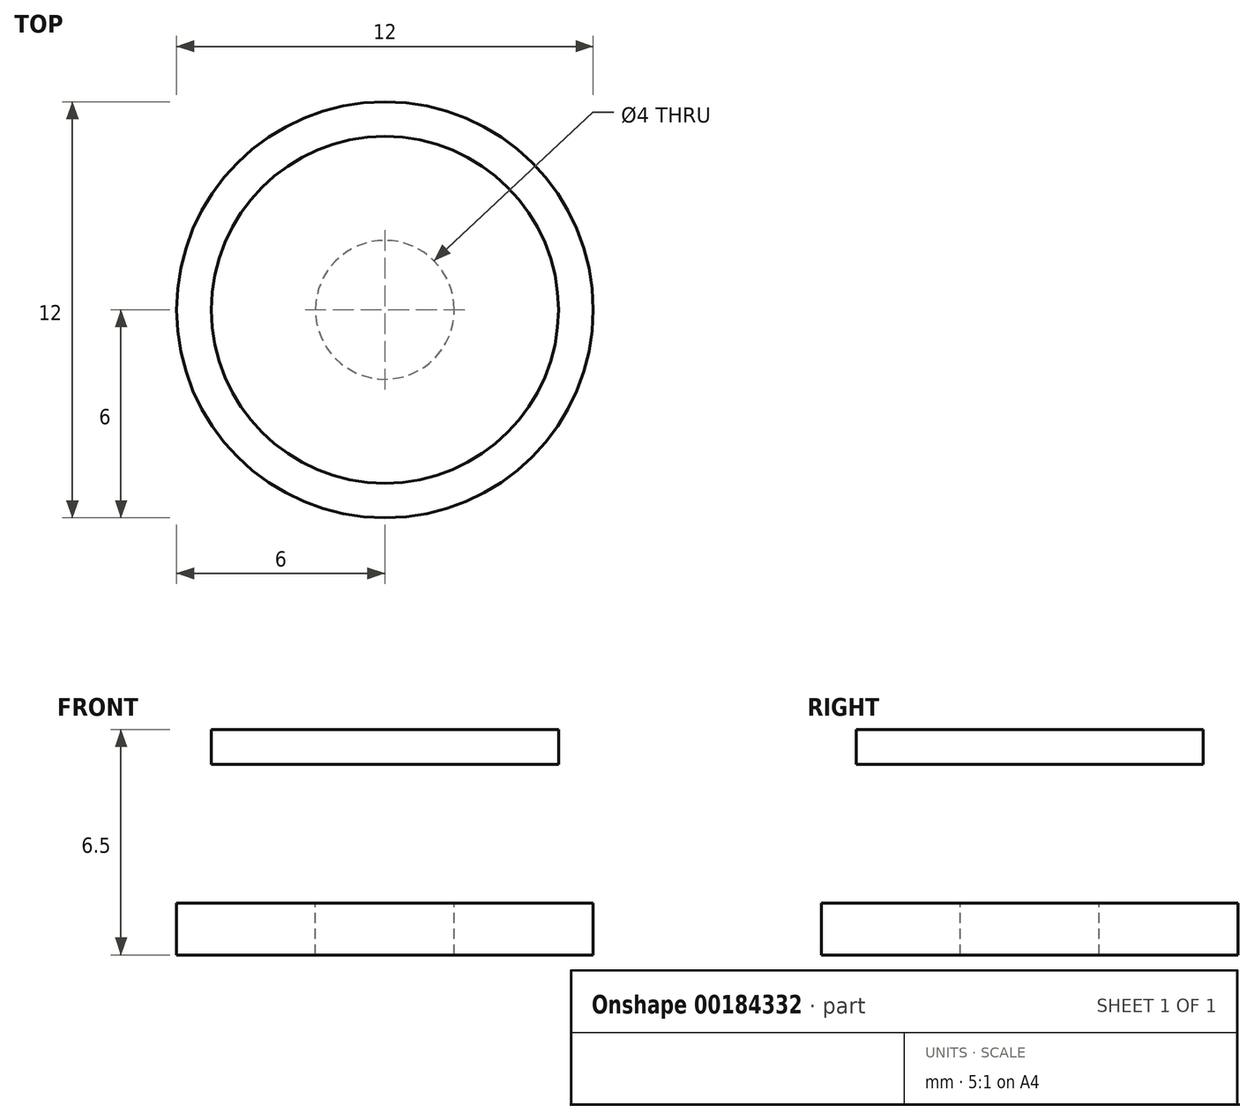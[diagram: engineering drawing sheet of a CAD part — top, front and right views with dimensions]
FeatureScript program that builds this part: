
annotation { "Feature Type Name" : "Feature", "Feature Type Description" : "" }
export const myFeature = defineFeature(function(context is Context, id is Id, definition is map)
    precondition{}
    {
        {
            var Q0;
            Q0=qCreatedBy(makeId("Right.planeOp"),FACE);
            var sketch = newSketch(context, id + "F0", { "sketchPlane" : qUnion([Q0])});
            skLineSegment(sketch, "E0.bottom", {"start": v(0, 0) * mm, "end": v(6, 0) * mm});
            skLineSegment(sketch, "E0.top", {"start": v(0, -1.5) * mm, "end": v(6, -1.5) * mm});
            skLineSegment(sketch, "E0.left", {"start": v(0, 0) * mm, "end": v(0, -1.5) * mm});
            skLineSegment(sketch, "E0.right", {"start": v(6, 0) * mm, "end": v(6, -1.5) * mm});
            skLineSegment(sketch, "E1.bottom", {"start": v(0, 0) * mm, "end": v(5, 0) * mm});
            skLineSegment(sketch, "E1.left", {"start": v(0, 0) * mm, "end": v(0, 4) * mm});
            skLineSegment(sketch, "E1.right", {"start": v(5, 0) * mm, "end": v(5, 4) * mm});
            skArc(sketch, "E2", {"start": v(5, 4) * mm, "mid": v(3, 2) * mm, "end": v(5, 0) * mm});
            skLineSegment(sketch, "E3.top", {"start": v(0, 5) * mm, "end": v(5, 5) * mm});
            skLineSegment(sketch, "E3.left", {"start": v(0, 4) * mm, "end": v(0, 5) * mm});
            skLineSegment(sketch, "E4", {"start": v(5, 4) * mm, "end": v(5, 5) * mm});
            skLineSegment(sketch, "E5", {"start": v(0, 4) * mm, "end": v(5, 4) * mm});
            skSolve(sketch);
        }
        {
            var Q0;
            Q0=makeQuery(id+"F0.imprint","IMPRINT",FACE,{"disambiguationData":[TD([[makeQuery(id+"F0.imprint","IMPRINT",EDGE,{"derivedFrom":sQuery(id+"F0.wireOp",EDGE,"E0.bottom")}),-1.0]])]});
            var Q1;
            Q1=makeQuery(id+"F0.imprint","IMPRINT",FACE,{"disambiguationData":[TD([[makeQuery(id+"F0.imprint","IMPRINT",EDGE,{"derivedFrom":sQuery(id+"F0.wireOp",EDGE,"E1.bottom")}),1.0]])]});
            var Q2;
            Q2=makeQuery(id+"F0.imprint","IMPRINT",FACE,{"disambiguationData":[TD([[makeQuery(id+"F0.imprint","IMPRINT",EDGE,{"derivedFrom":sQuery(id+"F0.wireOp",EDGE,"E3.top")}),-1.0]])]});
            var Q3;
            Q3=sQuery(id+"F0.wireOp",EDGE,"E1.left");
            revolve(context, id + "F1", {"entities" : qUnion([Q0, Q1, Q2]), "axis" : qUnion([Q3]), "revolveType" : RevolveType.FULL});
        }
        {
            var Q0;
            Q0=makeQuery(id+"F1.opRevolve","SWEPT_FACE",FACE,{"disambiguationData":[OSD([sQuery(id+"F0.wireOp",EDGE,"E3.top")])]});
            var sketch = newSketch(context, id + "F2", { "sketchPlane" : qUnion([Q0])});
            skPoint(sketch, "E6", {"position": v(0, 0) * mm});
            skSolve(sketch);
        }
        {
            var Q0;
            Q0=sQuery(id+"F2.wireOp",VERTEX,"E6");
            var Q1;
            Q1=makeQuery(id+"F1.opRevolve","SWEPT_BODY",BODY,{"disambiguationData":[OSD([sQuery(id+"F0.wireOp",EDGE,"E0.bottom"),sQuery(id+"F0.wireOp",EDGE,"E0.top"),sQuery(id+"F0.wireOp",EDGE,"E0.left"),sQuery(id+"F0.wireOp",EDGE,"E0.right"),sQuery(id+"F0.wireOp",EDGE,"E1.left"),sQuery(id+"F0.wireOp",EDGE,"E2"),sQuery(id+"F0.wireOp",EDGE,"E3.top"),sQuery(id+"F0.wireOp",EDGE,"E3.left"),sQuery(id+"F0.wireOp",EDGE,"E4")])]});
            hole(context, id + "F3", {"style" : HoleStyle.SIMPLE, "endStyle" : HoleEndStyle.THROUGH, "holeDiameter" : 4 * mm, "locations" : qUnion([Q0]), "scope" : qUnion([Q1]), "isTappedThrough" : true});
        }
    });
